# Revit family: assa_abloy_sw200i_14
name_source: partatom
category: Generic Models
units: mm (PartAtom-declared; Revit-internal decimal feet)

## family parameters
Always vertical = Yes
Can host rebar = No
Cut with Voids When Loaded = No
Host = Wall
Maintain Annotation Orientation = No
Part Type = Normal
Room Calculation Point = No
Round Connector Dimension = Use Diameter
Shared = No

## types (1)
- assa_abloy_sw200i_14
    BIMobject category = Swing Doors
    Closed Door Axis Distance = 1' - 0"
    Date of publishing = 2015-02-23
    Default Elevation = 0' - 0"
    Depth = 0.00
    Edition number = 1
    Header Length = 6' - 0"
    Header Material = Clear Anodized
    IFC Classification = Door
    Manufacturer name = Besam-North America
    Material main = Aluminium
    Nominal height = 0.00
    Nominal width = 0.00
    Opened Door Axis Distance = 0' - 0"
    Operator Arm Material = Clear Anodized
    Product Guid = a6d7597d-b5c2-4f9e-8316-3faa01ef08e4
    Product SKU = SW200i_SM
    Product data url = http://besam-na.bimobject.com
    Product family = Swing
    Product group = Surface Mount
    Pull Arm Guide Offset = 0' - 4 1/2"
    QR code = http://besam-na.bimobject.com
    UNSPSC Code = 30171511
    Uniclass 1.4 Code = L81323
    Uniclass 1.4 Description = Swings
    Weight Net (Kg) = 0

## geometry (parser evidence)
native form markers: Blend x2, Sweep x25
no freeform markers — native parametric forms only
